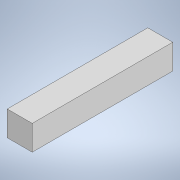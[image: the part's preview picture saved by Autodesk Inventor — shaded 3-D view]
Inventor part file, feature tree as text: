
AUTODESK INVENTOR PART (.ipt)
format: ipt  version: 2020.2 (Build 242310000, 310)  size: 89,088 bytes
history: native  units: mm
features: extrude x1, sketch x1
ambient origin geometry x8: Origin, YZ Plane, XZ Plane, XY Plane, X Axis, Y Axis, Z Axis, Center Point
bodies: Solid1 (feature_tree)
feature tree (2):
  extrude  "Extrusion1"  Depth=16.0mm
  sketch  "Sketch1"  dims[d0=16.0mm d1=16.0mm d2=90.0mm d3=0.0mm]
